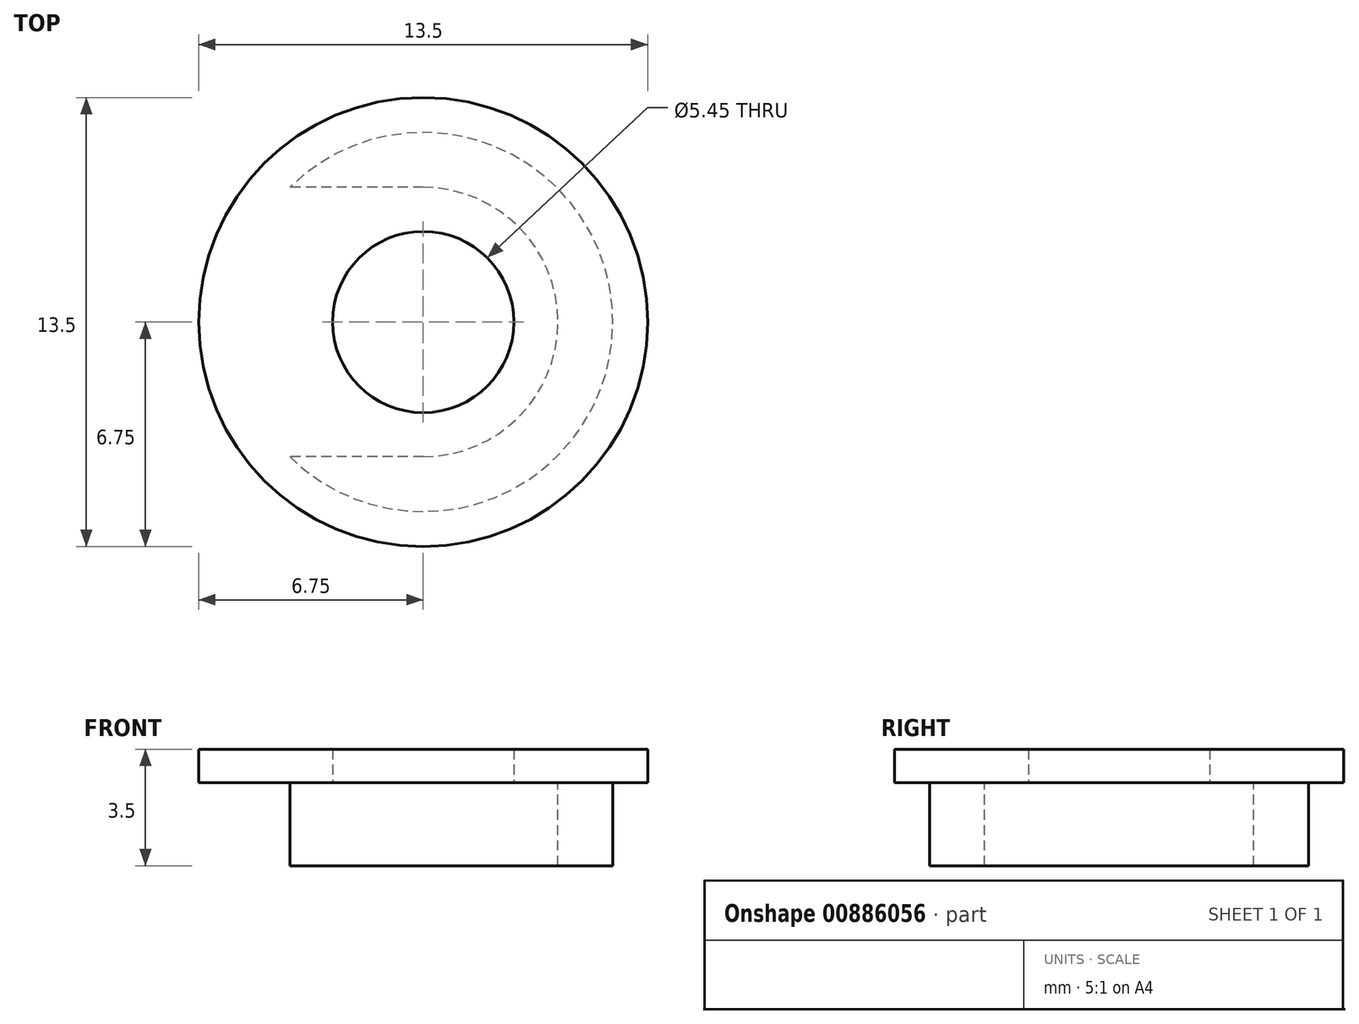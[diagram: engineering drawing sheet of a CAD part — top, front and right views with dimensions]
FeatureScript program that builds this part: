
annotation { "Feature Type Name" : "Feature", "Feature Type Description" : "" }
export const myFeature = defineFeature(function(context is Context, id is Id, definition is map)
    precondition{}
    {
        {
            var Q0;
            Q0=qCreatedBy(makeId("Top.planeOp"),FACE);
            var sketch = newSketch(context, id + "F0", { "sketchPlane" : qUnion([Q0])});
            skCircle(sketch, "E0", {"center": v(0, 0) * mm, "radius": 6.75 * mm});
            skCircle(sketch, "E1", {"center": v(0, 0) * mm, "radius": 2.73 * mm});
            skSolve(sketch);
        }
        {
            var Q0;
            Q0 = qSketchRegion(id + "F0", true);
            extrude(context, id + "F1", {"entities" : qUnion([Q0]), "depth" : 1 * mm, "offsetDistance" : 25 * mm});
        }
        {
            var Q0;
            Q0=makeQuery(id+"F1.opExtrude","CAP_FACE",FACE,{"disambiguationData":[OSD([sQuery(id+"F0.wireOp",EDGE,"E0"),sQuery(id+"F0.wireOp",EDGE,"E1")])],"isStart":true});
            var sketch = newSketch(context, id + "F2", { "sketchPlane" : qUnion([Q0])});
            skCircle(sketch, "E2", {"center": v(0, 0) * mm, "radius": 5.7 * mm});
            skCircle(sketch, "E3", {"center": v(0, 0) * mm, "radius": 4.05 * mm});
            skLineSegment(sketch, "E4.bottom", {"start": v(0, 4.05) * mm, "end": v(-6.75, 4.05) * mm});
            skLineSegment(sketch, "E4.top", {"start": v(0, -4.05) * mm, "end": v(-6.75, -4.05) * mm});
            skLineSegment(sketch, "E4.left", {"start": v(0, 4.05) * mm, "end": v(0, -4.05) * mm});
            skLineSegment(sketch, "E4.right", {"start": v(-6.75, 4.05) * mm, "end": v(-6.75, -4.05) * mm});
            skSolve(sketch);
        }
        {
            var Q0;
            {var subQ0=sQuery(id+"F2.wireOp",EDGE,"E4.bottom");var subQ1=sQuery(id+"F2.wireOp",EDGE,"E2");var subQ2=makeQuery(id+"F2.imprint","INTERSECT",VERTEX,{"derivedFrom":[subQ1,subQ0]});Q0=makeQuery(id+"F2.imprint","IMPRINT",FACE,{"disambiguationData":[TD([[makeQuery(id+"F2.imprint","IMPRINT",EDGE,{"disambiguationData":[TD([[subQ2,1.0]])],"derivedFrom":subQ1}),1.0]])]});}
            extrude(context, id + "F3", {"entities" : qUnion([Q0]), "operationType" : NewBodyOperationType.ADD, "depth" : 2.5 * mm, "offsetDistance" : 25 * mm});
        }
    });
